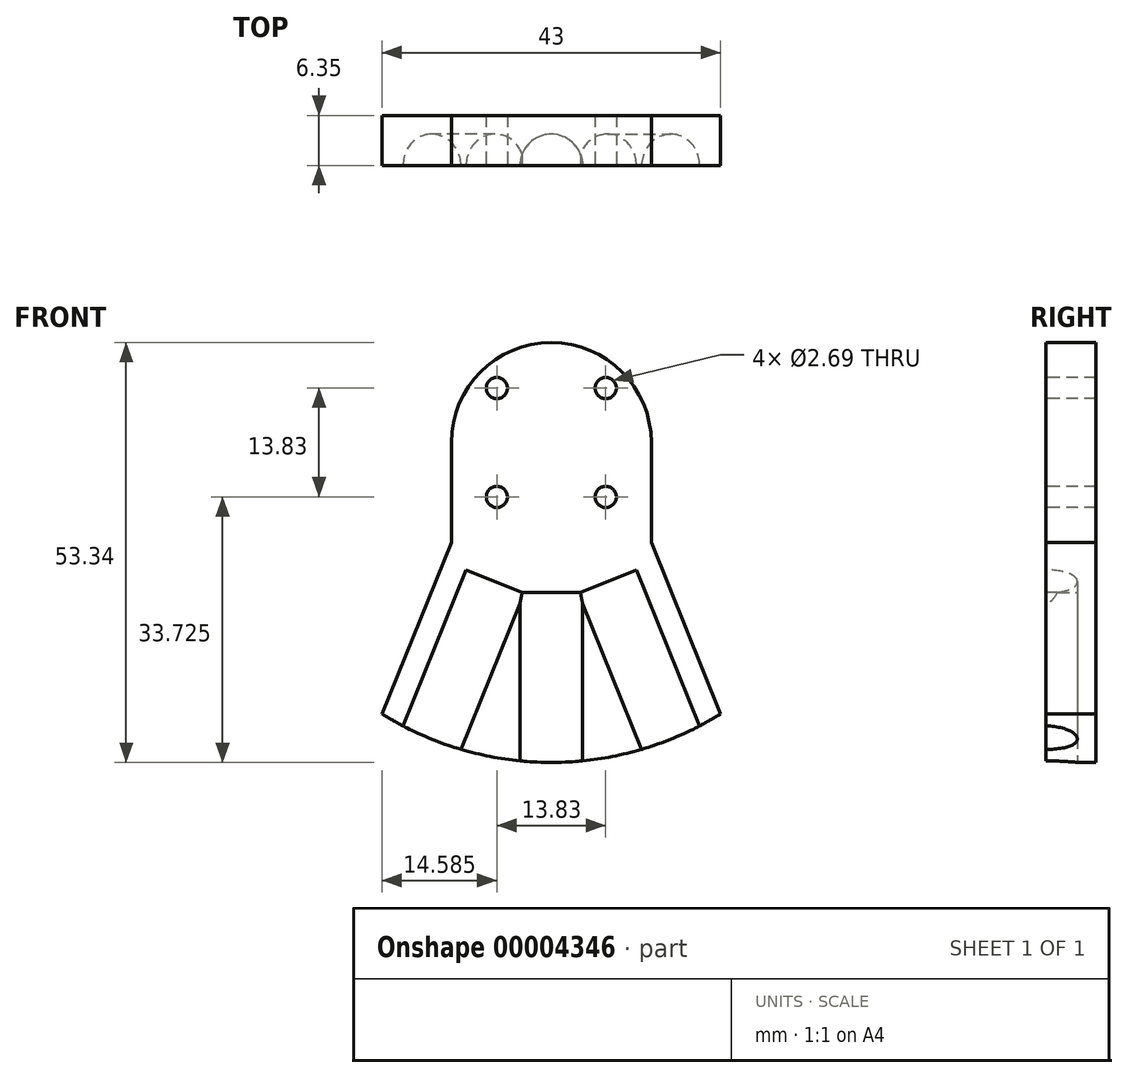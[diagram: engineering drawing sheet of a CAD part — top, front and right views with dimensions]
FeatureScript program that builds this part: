
annotation { "Feature Type Name" : "Feature", "Feature Type Description" : "" }
export const myFeature = defineFeature(function(context is Context, id is Id, definition is map)
    precondition{}
    {
        {
            var Q0;
            Q0=qCreatedBy(makeId("Front.planeOp"),FACE);
            var sketch = newSketch(context, id + "F0", { "sketchPlane" : qUnion([Q0])});
            skCircle(sketch, "E0", {"center": v(0, 0) * mm, "radius": 9.78 * mm, "construction": true});
            skCircle(sketch, "E1", {"center": v(0, 9.78) * mm, "radius": 1.35 * mm});
            skCircle(sketch, "E2.1.0", {"center": v(-6.91, 6.91) * mm, "radius": 1.35 * mm});
            skCircle(sketch, "E2.2.0", {"center": v(-9.78, 0) * mm, "radius": 1.35 * mm});
            skCircle(sketch, "E2.3.0", {"center": v(-6.91, -6.91) * mm, "radius": 1.35 * mm});
            skCircle(sketch, "E2.4.0", {"center": v(0, -9.78) * mm, "radius": 1.35 * mm});
            skCircle(sketch, "E2.5.0", {"center": v(6.91, -6.91) * mm, "radius": 1.35 * mm});
            skCircle(sketch, "E2.6.0", {"center": v(9.78, 0) * mm, "radius": 1.35 * mm});
            skCircle(sketch, "E2.7.0", {"center": v(6.91, 6.91) * mm, "radius": 1.35 * mm});
            skArc(sketch, "E3", {"start": v(0, 12.7) * mm, "mid": v(-8.98, 8.98) * mm, "end": v(-12.7, 0) * mm});
            skLineSegment(sketch, "E4", {"start": v(-12.7, 0) * mm, "end": v(-12.7, -12.7) * mm});
            skLineSegment(sketch, "E5", {"start": v(-12.7, -12.7) * mm, "end": v(-21.5, -34.49) * mm});
            skArc(sketch, "E6.0.MirrorCS", {"start": v(0, 12.7) * mm, "mid": v(8.98, 8.98) * mm, "end": v(12.7, 0) * mm});
            skLineSegment(sketch, "E7.0.MirrorCS", {"start": v(12.7, 0) * mm, "end": v(12.7, -12.7) * mm});
            skLineSegment(sketch, "E8.0.MirrorCS", {"start": v(12.7, -12.7) * mm, "end": v(21.5, -34.49) * mm});
            skLineSegment(sketch, "E9", {"start": v(-15.22, -37.68) * mm, "end": v(0, 0) * mm, "construction": true});
            skLineSegment(sketch, "E10", {"start": v(0, -40.64) * mm, "end": v(0, 0) * mm, "construction": true});
            skLineSegment(sketch, "E11", {"start": v(0, 0) * mm, "end": v(0, 0) * mm});
            skArc(sketch, "E12", {"start": v(-21.5, -34.49) * mm, "mid": v(-11.18, -39.07) * mm, "end": v(0, -40.64) * mm});
            skArc(sketch, "E13.0.MirrorCS", {"start": v(21.5, -34.49) * mm, "mid": v(11.18, -39.07) * mm, "end": v(0, -40.64) * mm});
            skArc(sketch, "E14", {"start": v(-7.14, -17.66) * mm, "mid": v(-3.63, -18.7) * mm, "end": v(0, -19.05) * mm, "construction": true});
            skLineSegment(sketch, "E15", {"start": v(0, -40.64) * mm, "end": v(0, -40.64) * mm});
            skLineSegment(sketch, "E16", {"start": v(0, -40.64) * mm, "end": v(23.99, -40.64) * mm, "construction": true});
            skLineSegment(sketch, "E17", {"start": v(21.5, -34.49) * mm, "end": v(23.99, -40.64) * mm, "construction": true});
            skPoint(sketch, "E18", {"position": v(22.7, -37.43) * mm});
            skSolve(sketch);
        }
        {
            var Q0;
            Q0=makeQuery(id+"F0.imprint","IMPRINT",FACE,{"disambiguationData":[TD([[makeQuery(id+"F0.imprint","IMPRINT",EDGE,{"derivedFrom":sQuery(id+"F0.wireOp",EDGE,"E1")}),-1.0]])]});
            var Q1;
            Q1=makeQuery(id+"F0.imprint","IMPRINT",FACE,{"disambiguationData":[TD([[makeQuery(id+"F0.imprint","IMPRINT",EDGE,{"derivedFrom":sQuery(id+"F0.wireOp",EDGE,"E2.4.0")}),1.0]])]});
            var Q2;
            Q2=makeQuery(id+"F0.imprint","IMPRINT",FACE,{"disambiguationData":[TD([[makeQuery(id+"F0.imprint","IMPRINT",EDGE,{"derivedFrom":sQuery(id+"F0.wireOp",EDGE,"E2.6.0")}),1.0]])]});
            var Q3;
            Q3=makeQuery(id+"F0.imprint","IMPRINT",FACE,{"disambiguationData":[TD([[makeQuery(id+"F0.imprint","IMPRINT",EDGE,{"derivedFrom":sQuery(id+"F0.wireOp",EDGE,"E2.2.0")}),1.0]])]});
            var Q4;
            Q4=makeQuery(id+"F0.imprint","IMPRINT",FACE,{"disambiguationData":[TD([[makeQuery(id+"F0.imprint","IMPRINT",EDGE,{"derivedFrom":sQuery(id+"F0.wireOp",EDGE,"E1")}),1.0]])]});
            extrude(context, id + "F1", {"entities" : qUnion([Q0, Q1, Q2, Q3, Q4]), "oppositeDirection" : true, "depth" : 6.35 * mm});
        }
        {
            var Q0;
            Q0=sQuery(id+"F0.wireOp",EDGE,"E9");
            var Q1;
            Q1=sQuery(id+"F0.wireOp",VERTEX,"E9.start");
            cPlane(context, id + "F2", {"entities" : qUnion([Q0, Q1]), "cplaneType" : CPlaneType.LINE_POINT, "offset" : 152.4 * mm, "width" : 152.4 * mm, "height" : 152.4 * mm});
        }
        {
            var Q0;
            Q0=sQuery(id+"F0.wireOp",EDGE,"E9");
            var Q1;
            Q1=sQuery(id+"F0.wireOp",VERTEX,"E14.start");
            cPlane(context, id + "F3", {"entities" : qUnion([Q0, Q1]), "cplaneType" : CPlaneType.LINE_POINT, "offset" : 152.4 * mm, "width" : 152.4 * mm, "height" : 152.4 * mm});
        }
        {
            var Q0;
            Q0=qCreatedBy(id+"F2.planeOp",FACE);
            var sketch = newSketch(context, id + "F4", { "sketchPlane" : qUnion([Q0])});
            skCircle(sketch, "E19", {"center": v(0, 0) * mm, "radius": 3.97 * mm});
            skSolve(sketch);
        }
        {
            var Q0;
            Q0=makeQuery(id+"F4.imprint","IMPRINT",FACE,{"disambiguationData":[TD([[makeQuery(id+"F4.imprint","IMPRINT",EDGE,{"derivedFrom":sQuery(id+"F4.wireOp",EDGE,"E19")}),1.0]])]});
            var Q1;
            Q1=qCreatedBy(id+"F3.planeOp",FACE);
            extrude(context, id + "F5", {"entities" : qUnion([Q0]), "endBound" : BoundingType.UP_TO_SURFACE, "endBoundEntityFace" : qUnion([Q1]), "depth" : 25.4 * mm, "hasSecondDirection" : true, "secondDirectionOppositeDirection" : true, "secondDirectionDepth" : 0.25 * mm});
        }
        {
            var Q0;
            Q0=makeQuery(id+"F5.opExtrude","SWEPT_BODY",BODY,{"disambiguationData":[OSD([sQuery(id+"F4.wireOp",EDGE,"E19")])]});
            var Q1;
            Q1=sQuery(id+"F0.wireOp",EDGE,"E12");
            circularPattern(context, id + "F6", {"entities" : qUnion([Q0]), "axis" : qUnion([Q1]), "angle" : 22 * degree, "instanceCount" : 3, "computeTransformsWithoutBuiltin" : true});
        }
        {
            var Q0;
            Q0=makeQuery(id+"F5.opExtrude","SWEPT_BODY",BODY,{"disambiguationData":[OSD([sQuery(id+"F4.wireOp",EDGE,"E19")])]});
            var Q1;
            Q1=makeQuery(id+"F6.opPattern","COPY",BODY,{"derivedFrom":makeQuery(id+"F5.opExtrude","SWEPT_BODY",BODY,{"disambiguationData":[OSD([sQuery(id+"F4.wireOp",EDGE,"E19")])]}),"instanceName":"1"});
            var Q2;
            Q2=makeQuery(id+"F6.opPattern","COPY",BODY,{"derivedFrom":makeQuery(id+"F5.opExtrude","SWEPT_BODY",BODY,{"disambiguationData":[OSD([sQuery(id+"F4.wireOp",EDGE,"E19")])]}),"instanceName":"2"});
            var Q3;
            Q3=makeQuery(id+"F1.opExtrude","SWEPT_BODY",BODY,{"disambiguationData":[OSD([sQuery(id+"F0.wireOp",EDGE,"E1"),sQuery(id+"F0.wireOp",EDGE,"E2.1.0"),sQuery(id+"F0.wireOp",EDGE,"E2.2.0"),sQuery(id+"F0.wireOp",EDGE,"E2.3.0"),sQuery(id+"F0.wireOp",EDGE,"E2.4.0"),sQuery(id+"F0.wireOp",EDGE,"E2.5.0"),sQuery(id+"F0.wireOp",EDGE,"E2.6.0"),sQuery(id+"F0.wireOp",EDGE,"E2.7.0"),sQuery(id+"F0.wireOp",EDGE,"E3"),sQuery(id+"F0.wireOp",EDGE,"E4"),sQuery(id+"F0.wireOp",EDGE,"E5"),sQuery(id+"F0.wireOp",EDGE,"95b1fc9c-570a-4565-b1ab-3f5467ce1071"),sQuery(id+"F0.wireOp",EDGE,"E6.0.MirrorCS"),sQuery(id+"F0.wireOp",EDGE,"E7.0.MirrorCS"),sQuery(id+"F0.wireOp",EDGE,"E8.0.MirrorCS"),sQuery(id+"F0.wireOp",EDGE,"22c72f58-c1fc-4741-9573-2fed90a28a41.0.MirrorCS")])]});
            booleanBodies(context, id + "F7", {"operationType" : BooleanOperationType.SUBTRACTION, "tools" : qUnion([Q0, Q1, Q2]), "targets" : qUnion([Q3])});
        }
    });
